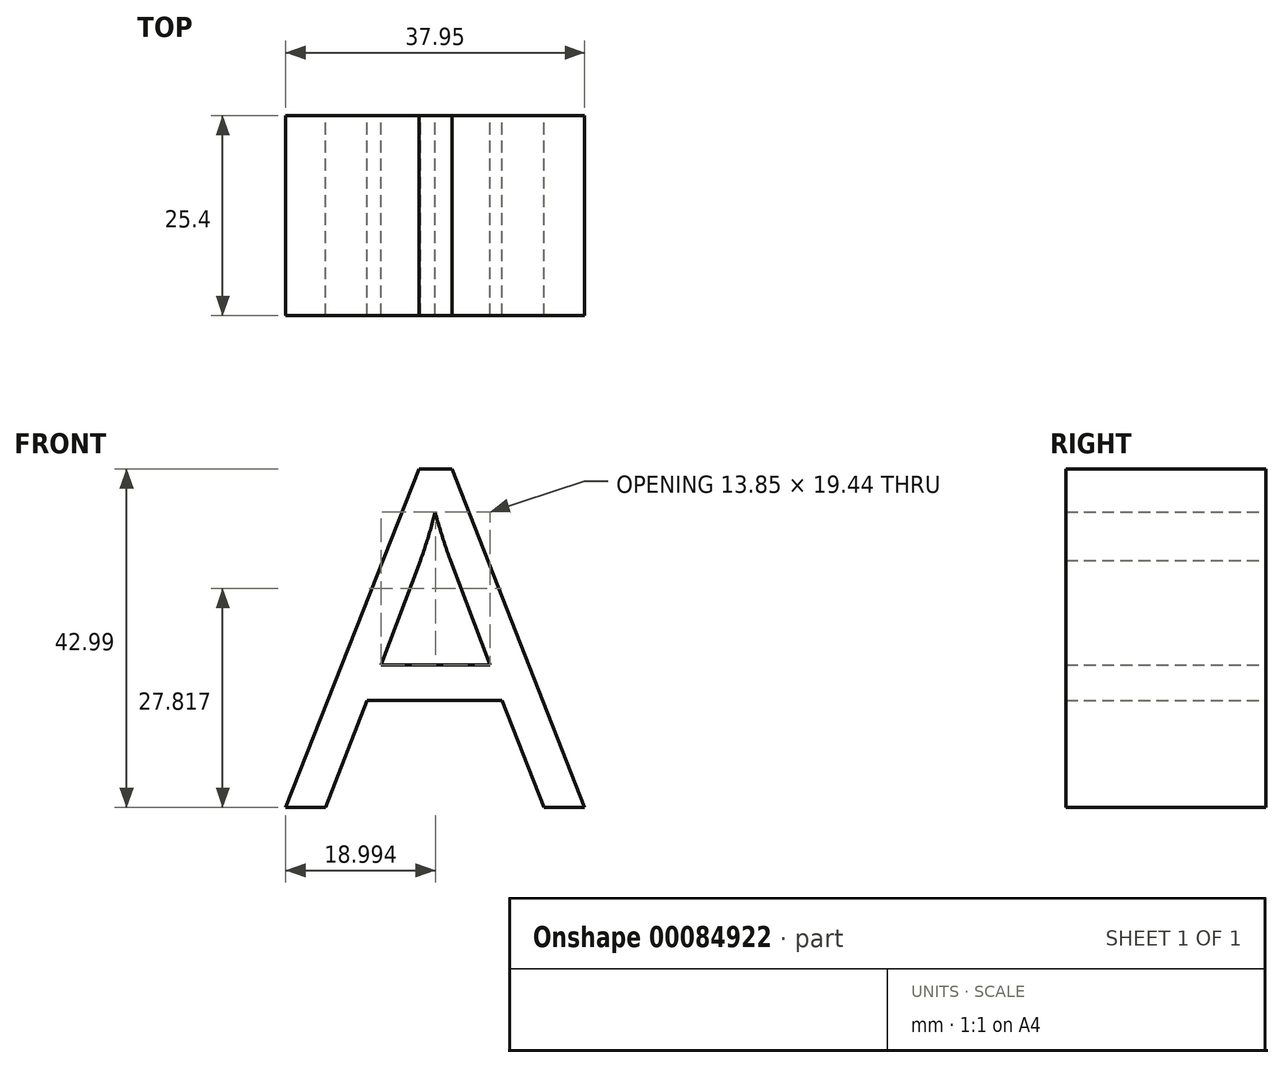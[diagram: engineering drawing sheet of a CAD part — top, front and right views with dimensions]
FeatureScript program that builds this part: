
annotation { "Feature Type Name" : "Feature", "Feature Type Description" : "" }
export const myFeature = defineFeature(function(context is Context, id is Id, definition is map)
    precondition{}
    {
        {
            var Q0;
            Q0=qCreatedBy(makeId("Front.planeOp"),FACE);
            var sketch = newSketch(context, id + "F0", { "sketchPlane" : qUnion([Q0])});
            skText(sketch, "E0", { "text": "A", "fontName": "OpenSans-Regular.ttf"});
            const initialGuessF0  = {"E0": [-0.03795, 0.0193, 1, 0, 0.04318]};
            skSetInitialGuess(sketch, initialGuessF0);
            skSolve(sketch);
        }
        {
            var Q0;
            Q0 = qSketchRegion(id + "F0", true);
            extrude(context, id + "F1", {"entities" : qUnion([Q0]), "depth" : 25.4 * mm});
        }
    });
